# Revit family: Sensor-Lutron-Wall_Mount-Occupancy-12ft-LOS-WDT
name_source: partatom
category: Lighting Devices
revit_build: Autodesk Revit 2017 (Build: 20160720_1515(x64)
units: mm (PartAtom-declared; Revit-internal decimal feet)

## family parameters
Cut with Voids When Loaded = No
Host = Face
Maintain Annotation Orientation = Yes
OmniClass Number = 23.85.80.11.27
OmniClass Title = Lighting Controls
Part Type = Normal
Room Calculation Point = No
Round Connector Dimension = Use Diameter
Shared = No

## types (2) — shared parameters
Assembly Code = D5030800
Coverage = 1600.00 SF
Description = Dual Technology Wall Mount Occupancy Sensor
Field of View = 110.00°
Height = 0' - 5 1/4"
Infrared Major Motion = 40' - 0"
Infrared Minor Motion = 20' - 0"
Instruction Sheet Link = http://www.lutron.com
Manufacturer = Lutron Electronics Co., Inc
Manufacturer Fax Number = 610-282-1243
Nominal Depth = 0' - 3 29/32"
Nominal Height = 0' - 6 13/32"
Nominal Width = 0' - 3 19/32"
Performance URL = http://www.lutron.com
Product Documentation Link = http://www.lutron.com
Product Name = Dual Technology Wall Mount Occupancy Sensor
Product Page URL = http://www.lutron.com
Range Diagram Height = 12' - 0"
Sensor Material = Plastic-Lutron-White-Gloss
Series = LOS-W
URL = http://www.lutron.com
Ultrasonic Major Motion = 32' - 0"
Ultrasonic Minor Motion = 23' - 0"
Version = 2017 - v1.0b
Video Link = https://www.youtube.com
Voltage Comments = 20-24VDC
Warranty URL = http://www.lutron.com
zero-valued in all types: Cost

## per-type parameters (varying)
| type | Default Elevation |
| LOS-WDT-R-WH | 6' - 0" |
| LOS-WDT-WH | 8' - 0" |

note: column(s) folded — value = type name in every type: Model

## geometry (parser evidence)
native form markers: Sweep x2
no freeform markers — native parametric forms only
